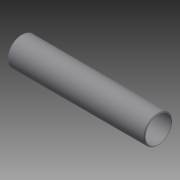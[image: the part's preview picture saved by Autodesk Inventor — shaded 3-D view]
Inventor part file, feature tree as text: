
AUTODESK INVENTOR PART (.ipt)
format: ipt  version: 2014 SP2 (Build 180246200, 246)  size: 142,336 bytes
history: native  units: in
note: dims shown in document units (in); Inventor stores cm internally (conversion verified against a paired STEP export)
features: other x42, revolve x1, sketch x1
ambient origin geometry x8: Origin, YZ Plane, XZ Plane, XY Plane, X Axis, Y Axis, Z Axis, Center Point
bodies: Solid1 (feature_tree)
feature tree (44):
  revolve  "Revolution1"  [1 undecoded]
  other  "cp1_XY"
  other  "cp1_YZ"
  other  "cp1_ZX"
  other  "cp1_X"
  other  "cp1_Y"
  other  "cp1_Z"
  other  "cp1_Center"
  other  "cp2_XY"
  other  "cp2_YZ"
  other  "cp2_ZX"
  other  "cp2_X"
  other  "cp2_Y"
  other  "cp2_Z"
  other  "cp2_Center"
  other  "cp3_XY"
  other  "cp3_YZ"
  other  "cp3_ZX"
  other  "cp3_X"
  other  "cp3_Y"
  other  "cp3_Z"
  other  "cp3_Center"
  other  "cp4_XY"
  other  "cp4_YZ"
  other  "cp4_ZX"
  other  "cp4_X"
  other  "cp4_Y"
  other  "cp4_Z"
  other  "cp4_Center"
  other  "tube_front_XY"
  other  "tube_front_YZ"
  other  "tube_front_ZX"
  other  "tube_front_X"
  other  "tube_front_Y"
  other  "tube_front_Z"
  other  "tube_front_Center"
  other  "tube_rear_XY"
  other  "tube_rear_YZ"
  other  "tube_rear_ZX"
  other  "tube_rear_X"
  other  "tube_rear_Y"
  other  "tube_rear_Z"
  other  "tube_rear_Center"
  sketch  "Sketch_1"  dims[d0=360.0deg]
note: 1 required parameter value undecoded (feature->parameter linkage not recoverable at this tier; creation-order binding heuristic only, values carry confidence <= 0.55)
